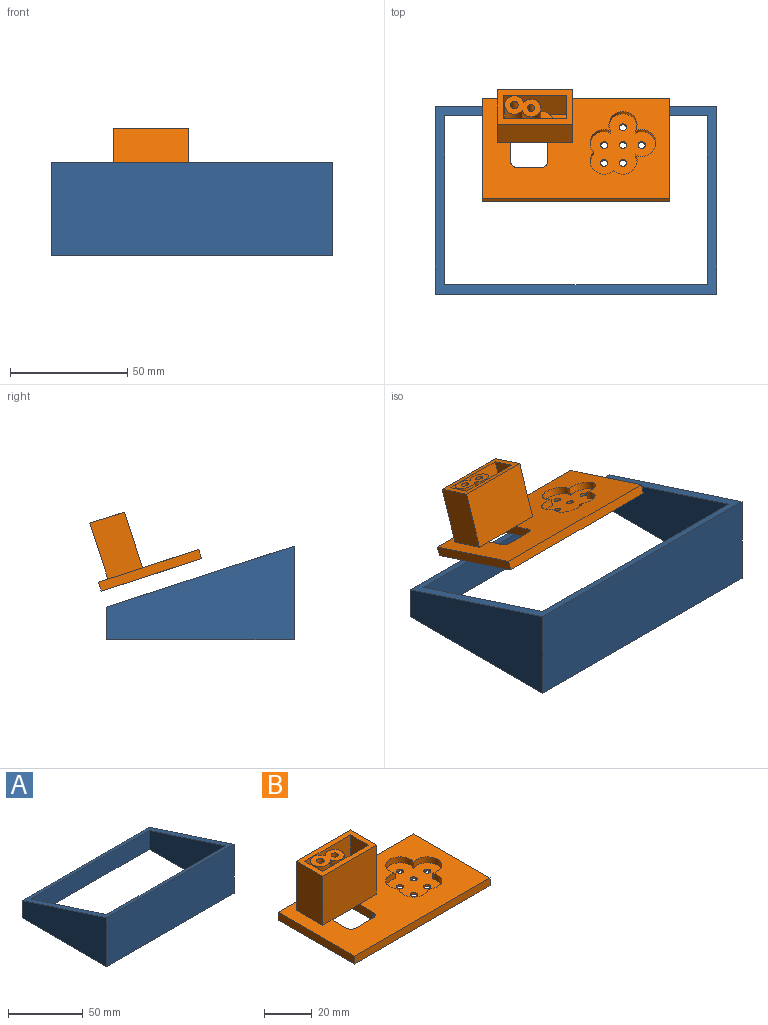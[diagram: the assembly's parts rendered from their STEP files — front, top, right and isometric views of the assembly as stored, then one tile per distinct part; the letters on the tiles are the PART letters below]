
ASSEMBLY  parts=2 mates=1
PART A: 10 faces, bbox 120x80x40 mm
  f0: plane 120x14mm, normal (0,1,0), area 1680mm2, adj f1,f3,f4,f9
  f1: plane 120x80mm, normal (0,0,-1), area 1536mm2, adj f0,f2,f3,f4,f5,f6,f7,f8
  f2: plane 120x40mm, normal (0,-1,0), area 4800mm2, adj f1,f3,f4,f9
  f3: plane 80x40mm, normal (1,0,0), area 2160mm2, adj f0,f1,f2,f9
  f4: plane 80x40mm, normal (-1,0,0), area 2160mm2, adj f0,f1,f2,f9
  f5: plane 112x38.7mm, normal (0,1,0), area 4334.4mm2, adj f1,f6,f8,f9
  f6: plane 72x38.7mm, normal (-1,0,0), area 1944mm2, adj f1,f5,f7,f9
  f7: plane 112x15.3mm, normal (0,-1,0), area 1713.6mm2, adj f1,f6,f8,f9
  f8: plane 72x38.7mm, normal (1,0,0), area 1944mm2, adj f1,f5,f7,f9
  f9: plane 120x80mm, normal (0,0.31,0.95), area 1615.1mm2, adj f0,f2,f3,f4,f5,f6,f7,f8
PART B: 50 faces, bbox 80x45x29 mm
  f0: plane 15.38x9.44mm, normal (0,0,1), area 86.8mm2, adj f34,f35,f48,f49
  f1: cylinder r=3mm len=4mm, axis (0,0,1), area 2.7mm2, adj f4,f22,f33,f35
  f2: cylinder r=3mm len=4mm, axis (0,0,1), area 8.2mm2, adj f4,f21,f33,f35
  f3: plane 80x45mm, normal (0,0,1), area 2401.2mm2, adj f11,f12,f13,f14,f16,f17,f18,f19
  f4: plane 80x45mm, normal (0,0,-1), area 3213.1mm2, adj f1,f2,f5,f6,f7,f8,f9,f10
  f5: cylinder r=1.5mm len=3mm, axis (0,0,1), area 9.4mm2, adj f4,f15
  f6: cylinder r=1.5mm len=3mm, axis (0,0,1), area 9.4mm2, adj f4,f15
  f7: cylinder r=1.5mm len=3mm, axis (0,0,1), area 9.4mm2, adj f4,f15
  f8: cylinder r=1.5mm len=3mm, axis (0,0,1), area 9.4mm2, adj f4,f15
  f9: cylinder r=1.5mm len=3mm, axis (0,0,1), area 9.4mm2, adj f4,f15
  f10: cylinder r=1.5mm len=3mm, axis (0,0,1), area 9.4mm2, adj f4,f15
  f11: plane 80x4mm, normal (0,-1,0), area 320mm2, adj f3,f4,f12,f14
  f12: plane 45x4mm, normal (1,0,0), area 180mm2, adj f3,f4,f11,f13
  f13: plane 80x4mm, normal (0,1,0), area 320mm2, adj f3,f4,f12,f14
  f14: plane 45x4mm, normal (-1,0,0), area 180mm2, adj f3,f4,f11,f13
  f15: plane 28x28mm, normal (0,0,1), area 485.9mm2, adj f5,f6,f7,f8,f9,f10,f16,f17
  f16: cylinder r=6mm len=12mm, axis (0,0,1), area 72.6mm2, adj f3,f15,f17,f20
  f17: cylinder r=6mm len=12mm, axis (0,0,1), area 72.6mm2, adj f3,f15,f16,f18
  f18: cylinder r=6mm len=10mm, axis (0,0,1), area 49.4mm2, adj f3,f15,f17,f19
  f19: cylinder r=6mm len=10mm, axis (0,0,1), area 54.5mm2, adj f3,f15,f18,f20
  f20: cylinder r=6mm len=10mm, axis (0,0,1), area 49.4mm2, adj f3,f15,f16,f19
  f21: plane 10x4mm, normal (0,-1,0), area 40mm2, adj f2,f4,f27,f33
  f22: plane 16x4mm, normal (1,0,0), area 64mm2, adj f1,f3,f4,f25,f33
  f23: plane 10x4mm, normal (0,1,0), area 40mm2, adj f3,f4,f25,f26
  f24: plane 16x4mm, normal (-1,0,0), area 64mm2, adj f3,f4,f26,f27,f33
  f25: cylinder r=3mm len=4mm, axis (0,0,-1), area 18.8mm2, adj f3,f4,f22,f23
  f26: cylinder r=3mm len=4mm, axis (0,0,1), area 18.8mm2, adj f3,f4,f23,f24
  f27: cylinder r=3mm len=4mm, axis (0,0,-1), area 18.8mm2, adj f4,f21,f24,f33
  f28: plane 25x15.5mm, normal (-1,0,0), area 387.6mm2, adj f3,f29,f31,f32
  f29: plane 31.99x25mm, normal (0,-1,0), area 799.7mm2, adj f3,f28,f30,f32,f33
  f30: plane 25x15.5mm, normal (1,0,0), area 387.6mm2, adj f3,f29,f31,f32
  f31: plane 31.99x25mm, normal (0,1,0), area 799.7mm2, adj f3,f28,f30,f32
  f32: plane 31.99x15.5mm, normal (0,0,1), area 212.4mm2, adj f28,f29,f30,f31,f36,f38,f39,f40
  f33: plane 16x10.85mm, normal (0,0,-1), area 154.3mm2, adj f1,f2,f21,f22,f24,f27,f29,f34
  f34: cylinder r=1.5mm len=25mm, axis (0,0,1), area 235.6mm2, adj f0,f33
  f35: cylinder r=1.65mm len=29mm, axis (0,0,1), area 267.5mm2, adj f0,f1,f2,f4,f33
  f36: plane 26.99x26.5mm, normal (0,-1,0), area 659.8mm2, adj f32,f37,f38,f39,f42,f43,f46,f47
  f37: plane 10.5x9mm, normal (0,0,1), area 61.9mm2, adj f36,f39,f40,f45,f46
  f38: plane 26.5x10.5mm, normal (1,0,0), area 278.3mm2, adj f32,f36,f40,f43
  f39: plane 26.5x10.5mm, normal (-1,0,0), area 278.3mm2, adj f32,f36,f37,f40
  f40: plane 26.99x26.5mm, normal (0,1,0), area 631.1mm2, adj f32,f37,f38,f39,f43,f44,f45,f47
  f41: cylinder r=5.5mm len=4mm, axis (0,0,1), area 3.6mm2, adj f43,f44,f47,f49
  f42: cylinder r=5.5mm len=4mm, axis (0,0,1), area 5.9mm2, adj f36,f43,f47,f49
  f43: plane 10.5x4.16mm, normal (0,0,1), area 10.6mm2, adj f36,f38,f40,f41,f42,f44,f49
  f44: plane 5.35x4mm, normal (-1,0,0), area 21.4mm2, adj f40,f41,f43,f47
  f45: plane 5.35x4mm, normal (1,0,0), area 21.4mm2, adj f37,f40,f46,f47
  f46: cylinder r=5.5mm len=5.16mm, axis (0,0,-1), area 26.7mm2, adj f36,f37,f45,f47
  f47: plane 21x10.5mm, normal (0,0,1), area 108.4mm2, adj f36,f40,f41,f42,f44,f45,f46,f48
  f48: cylinder r=4mm len=22.5mm, axis (0,0,1), area 483.3mm2, adj f0,f47,f49
  f49: cylinder r=4.15mm len=26.5mm, axis (0,0,1), area 522.3mm2, adj f0,f41,f42,f43,f47,f48
PLACE A at identity fixed
PLACE B rot(axis=(-1,0,0),18deg) t=(0,20.81,27.74)mm
MATE slider B.f4 <-> A.f9  axis (0,-0.31,-0.95) through (0,42.21,20.79)mm
